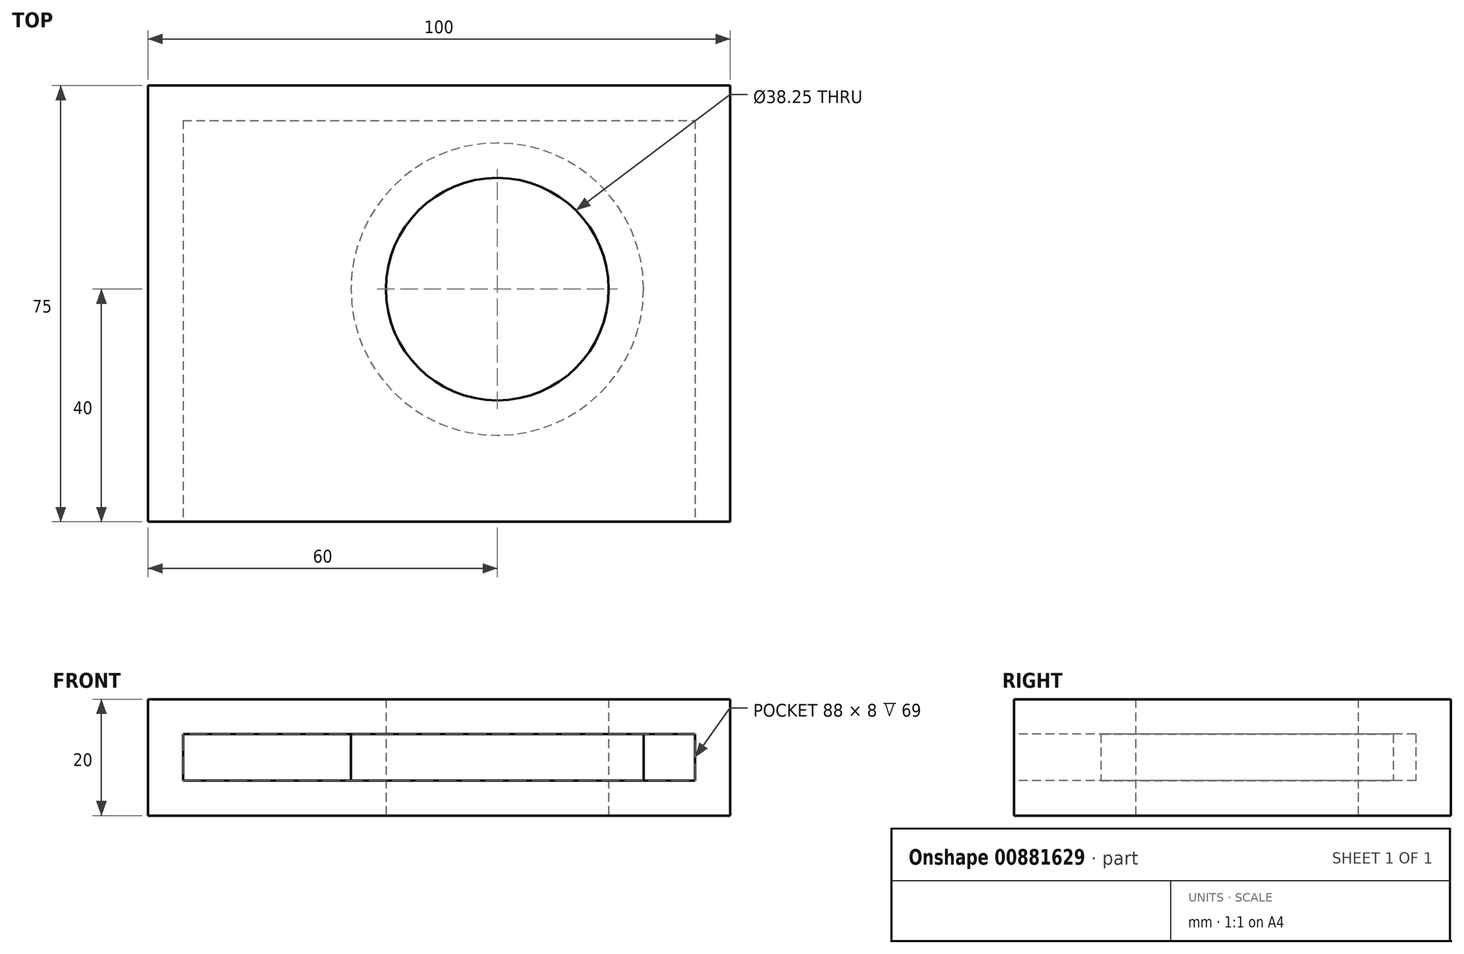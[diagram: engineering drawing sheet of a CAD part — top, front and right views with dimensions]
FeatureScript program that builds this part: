
annotation { "Feature Type Name" : "Feature", "Feature Type Description" : "" }
export const myFeature = defineFeature(function(context is Context, id is Id, definition is map)
    precondition{}
    {
        {
            var Q0;
            Q0=qCreatedBy(makeId("Top.planeOp"),FACE);
            var sketch = newSketch(context, id + "F0", { "sketchPlane" : qUnion([Q0])});
            skLineSegment(sketch, "E0.bottom", {"start": v(0, 0) * mm, "end": v(100, 0) * mm});
            skLineSegment(sketch, "E0.top", {"start": v(0, -75) * mm, "end": v(100, -75) * mm});
            skLineSegment(sketch, "E0.left", {"start": v(0, 0) * mm, "end": v(0, -75) * mm});
            skLineSegment(sketch, "E0.right", {"start": v(100, 0) * mm, "end": v(100, -75) * mm});
            skCircle(sketch, "E1", {"center": v(60, -35) * mm, "radius": 19.12 * mm});
            skSolve(sketch);
        }
        {
            var Q0;
            Q0=makeQuery(id+"F0.imprint","IMPRINT",FACE,{"disambiguationData":[TD([[makeQuery(id+"F0.imprint","IMPRINT",EDGE,{"derivedFrom":sQuery(id+"F0.wireOp",EDGE,"E0.bottom")}),-1.0]])]});
            extrude(context, id + "F1", {"entities" : qUnion([Q0]), "depth" : 20 * mm, "offsetDistance" : 25 * mm});
        }
        {
            var Q0;
            Q0=makeQuery(id+"F1.opExtrude","SWEPT_FACE",FACE,{"disambiguationData":[OSD([sQuery(id+"F0.wireOp",EDGE,"E0.top")])]});
            shell(context, id + "F2", {"entities" : qUnion([Q0]), "thickness" : 6 * mm});
        }
    });
